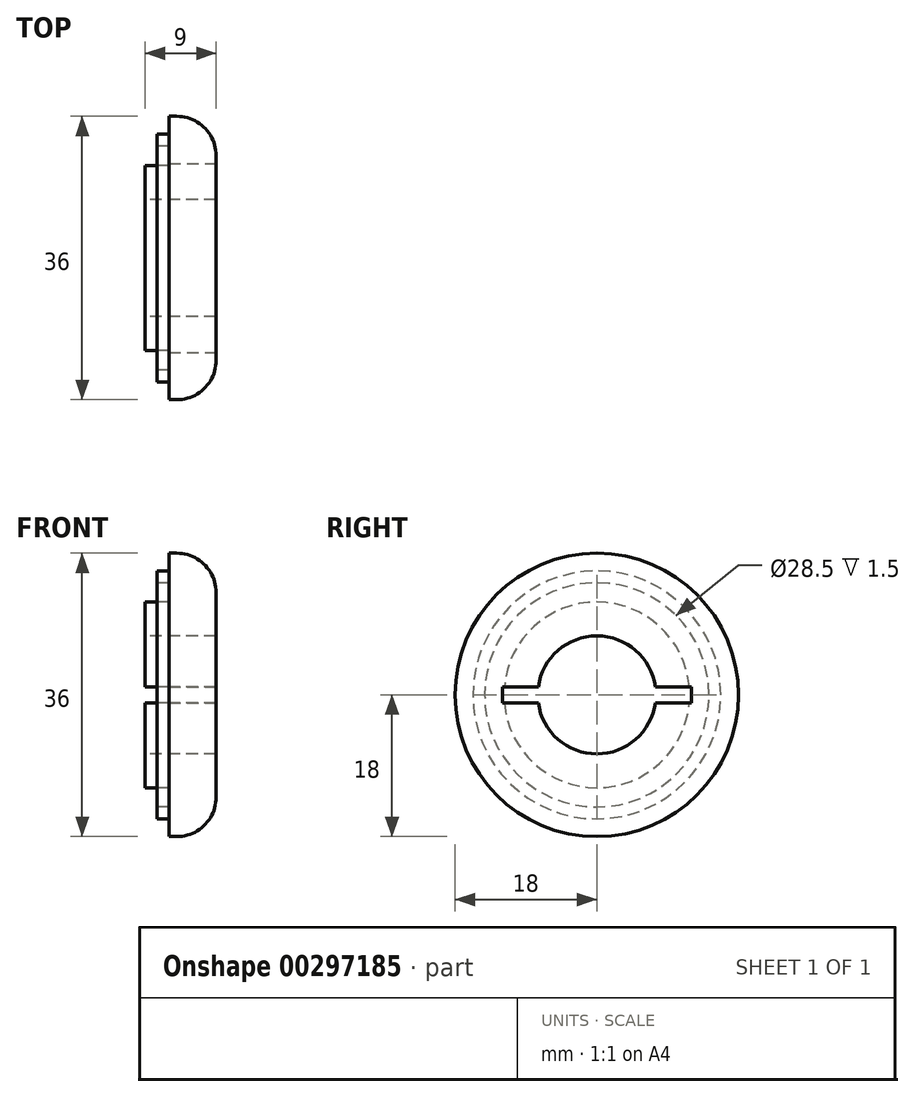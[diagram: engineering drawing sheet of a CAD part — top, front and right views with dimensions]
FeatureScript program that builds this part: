
annotation { "Feature Type Name" : "Feature", "Feature Type Description" : "" }
export const myFeature = defineFeature(function(context is Context, id is Id, definition is map)
    precondition{}
    {
        {
            var Q0;
            Q0=qCreatedBy(makeId("Front.planeOp"),FACE);
            var sketch = newSketch(context, id + "F0", { "sketchPlane" : qUnion([Q0])});
            skLineSegment(sketch, "E0", {"start": v(0, 7.5) * mm, "end": v(0, 11.8) * mm});
            skLineSegment(sketch, "E1", {"start": v(0, 11.8) * mm, "end": v(3, 11.8) * mm});
            skLineSegment(sketch, "E2", {"start": v(3, 11.8) * mm, "end": v(3, 14.25) * mm});
            skLineSegment(sketch, "E3", {"start": v(3, 14.25) * mm, "end": v(1.5, 14.25) * mm});
            skLineSegment(sketch, "E4", {"start": v(1.5, 14.25) * mm, "end": v(1.5, 15.75) * mm});
            skLineSegment(sketch, "E5", {"start": v(1.5, 15.75) * mm, "end": v(3, 15.75) * mm});
            skLineSegment(sketch, "E6", {"start": v(3, 15.75) * mm, "end": v(3, 18) * mm});
            skLineSegment(sketch, "E7", {"start": v(3, 18) * mm, "end": v(9, 18) * mm});
            skLineSegment(sketch, "E8", {"start": v(9, 18) * mm, "end": v(9, 7.5) * mm});
            skLineSegment(sketch, "E9", {"start": v(9, 7.5) * mm, "end": v(0, 7.5) * mm});
            skLineSegment(sketch, "E10", {"start": v(0, 7.5) * mm, "end": v(0, 0) * mm});
            skLineSegment(sketch, "E11", {"start": v(0, 0) * mm, "end": v(9, 0) * mm});
            skLineSegment(sketch, "E12", {"start": v(9, 0) * mm, "end": v(9, 7.5) * mm});
            skPoint(sketch, "E13", {"position": v(1.5, 15) * mm});
            skSolve(sketch);
        }
        {
            var Q0;
            Q0=makeQuery(id+"F0.imprint","IMPRINT",FACE,{"disambiguationData":[TD([[makeQuery(id+"F0.imprint","IMPRINT",EDGE,{"derivedFrom":sQuery(id+"F0.wireOp",EDGE,"E0")}),-1.0]])]});
            var Q1;
            Q1=sQuery(id+"F0.wireOp",EDGE,"E11");
            revolve(context, id + "F1", {"entities" : qUnion([Q0]), "axis" : qUnion([Q1]), "revolveType" : RevolveType.FULL});
        }
        {
            var Q0;
            Q0=makeQuery(id+"F1.opRevolve","SWEPT_EDGE",EDGE,{"disambiguationData":[OSD([sQuery(id+"F0.wireOp",EDGE,"E7"),sQuery(id+"F0.wireOp",EDGE,"E8")])]});
            fillet(context, id + "F2", {"entities" : qUnion([Q0]), "radius" : 5 * mm, "tangentPropagation" : true, "allowEdgeOverflow" : false});
        }
        {
            var Q0;
            Q0=makeQuery(id+"F1.opRevolve","SWEPT_FACE",FACE,{"disambiguationData":[OSD([sQuery(id+"F0.wireOp",EDGE,"E8")])]});
            var sketch = newSketch(context, id + "F3", { "sketchPlane" : qUnion([Q0])});
            skLineSegment(sketch, "E14.bottom", {"start": v(-12, 1) * mm, "end": v(12, 1) * mm});
            skLineSegment(sketch, "E14.top", {"start": v(-12, -1) * mm, "end": v(12, -1) * mm});
            skLineSegment(sketch, "E14.left", {"start": v(-12, 1) * mm, "end": v(-12, -1) * mm});
            skLineSegment(sketch, "E14.right", {"start": v(12, 1) * mm, "end": v(12, -1) * mm});
            skPoint(sketch, "E14.middle", {"position": v(0, 0) * mm});
            skSolve(sketch);
        }
        {
            var Q0;
            {var subQ0=sQuery(id+"F3.wireOp",EDGE,"E14.left");Q0=makeQuery(id+"F3.imprint","IMPRINT",FACE,{"disambiguationData":[TD([[makeQuery(id+"F3.imprint","IMPRINT",EDGE,{"derivedFrom":subQ0}),1.0]])]});}
            var Q1;
            {var subQ0=sQuery(id+"F3.wireOp",EDGE,"E14.bottom");var subQ1=makeQuery(id+"F1.opRevolve","SWEPT_EDGE",EDGE,{"disambiguationData":[OSD([sQuery(id+"F0.wireOp",EDGE,"E8"),sQuery(id+"F0.wireOp",EDGE,"E9"),sQuery(id+"F0.wireOp",EDGE,"E12")])]});var subQ2=makeQuery(id+"F3.imprint","INTERSECT",VERTEX,{"disambiguationData":[OD(0.0)],"derivedFrom":[subQ1,subQ0]});Q1=makeQuery(id+"F3.imprint","IMPRINT",FACE,{"disambiguationData":[TD([[makeQuery(id+"F3.imprint","IMPRINT",EDGE,{"disambiguationData":[TD([[subQ2,-1.0]])],"derivedFrom":subQ0}),-1.0]])]});}
            var Q2;
            {var subQ0=sQuery(id+"F3.wireOp",EDGE,"E14.right");Q2=makeQuery(id+"F3.imprint","IMPRINT",FACE,{"disambiguationData":[TD([[makeQuery(id+"F3.imprint","IMPRINT",EDGE,{"derivedFrom":subQ0}),-1.0]])]});}
            extrude(context, id + "F4", {"entities" : qUnion([Q0, Q1, Q2]), "operationType" : NewBodyOperationType.REMOVE, "endBound" : BoundingType.THROUGH_ALL, "oppositeDirection" : true, "depth" : 25 * mm, "offsetDistance" : 25 * mm});
        }
    });
